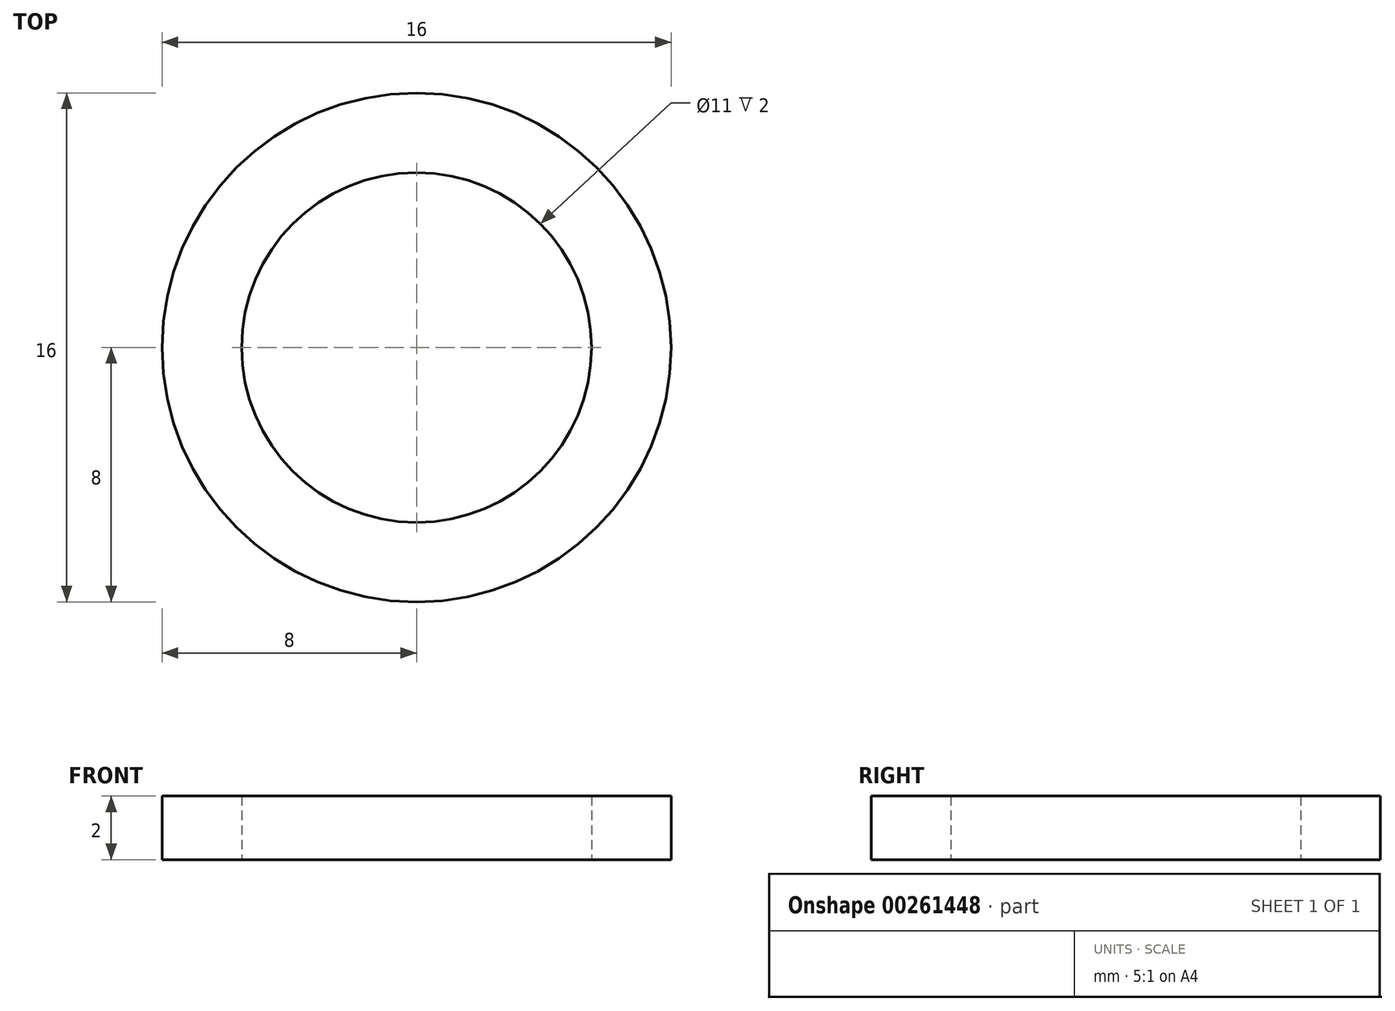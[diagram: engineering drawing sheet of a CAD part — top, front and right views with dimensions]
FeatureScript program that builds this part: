
annotation { "Feature Type Name" : "Feature", "Feature Type Description" : "" }
export const myFeature = defineFeature(function(context is Context, id is Id, definition is map)
    precondition{}
    {
        {
            var Q0;
            Q0=qCreatedBy(makeId("Top.planeOp"),FACE);
            var sketch = newSketch(context, id + "F0", { "sketchPlane" : qUnion([Q0])});
            skCircle(sketch, "E0", {"center": v(0, 0) * mm, "radius": 5.5 * mm});
            skCircle(sketch, "E1", {"center": v(0, 0) * mm, "radius": 8 * mm});
            skSolve(sketch);
        }
        {
            var Q0;
            Q0=qSketchRegion(id+"F0",true);
            extrude(context, id + "F1", {"entities" : qUnion([Q0]), "depth" : 2 * mm});
        }
    });
